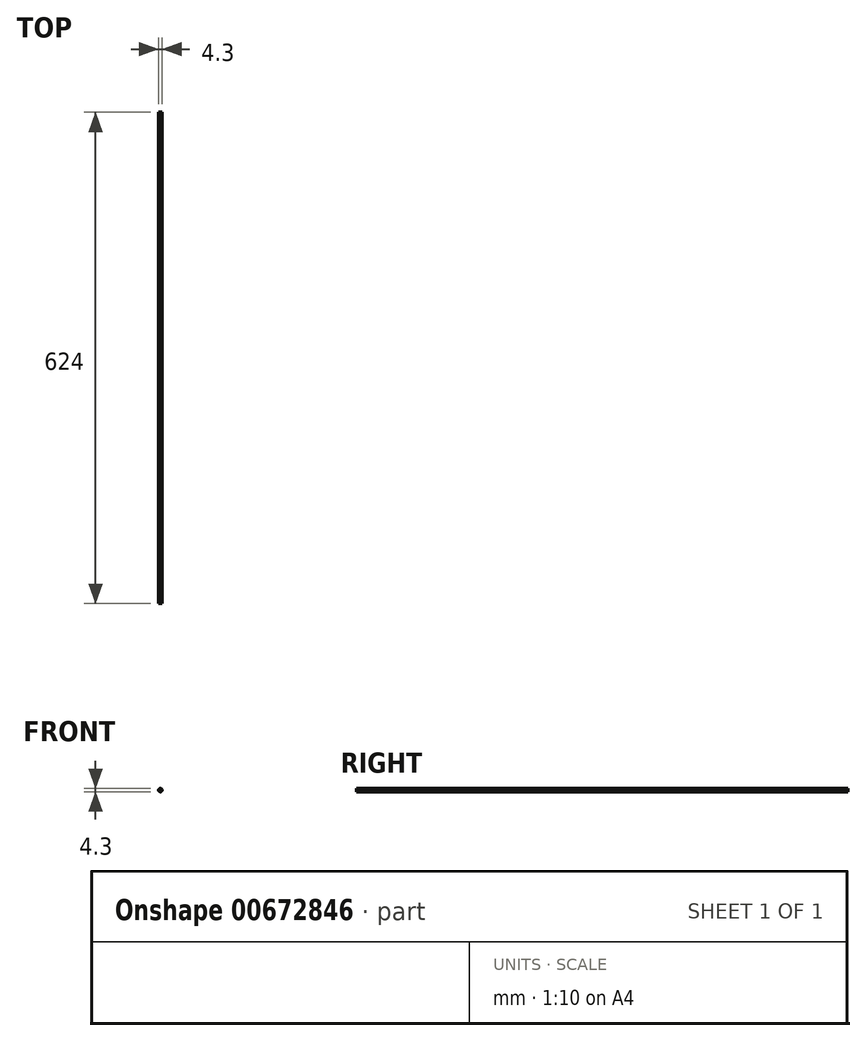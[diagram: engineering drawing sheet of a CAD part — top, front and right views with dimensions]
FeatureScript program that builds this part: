
annotation { "Feature Type Name" : "Feature", "Feature Type Description" : "" }
export const myFeature = defineFeature(function(context is Context, id is Id, definition is map)
    precondition{}
    {
        {
            var Q0;
            Q0=qCreatedBy(makeId("Front.planeOp"),FACE);
            var sketch = newSketch(context, id + "F0", { "sketchPlane" : qUnion([Q0])});
            skCircle(sketch, "E0", {"center": v(0.34, 6.3) * mm, "radius": 2.15 * mm});
            skLineSegment(sketch, "E1", {"start": v(4.5, 11.25) * mm, "end": v(4.5, 14.5) * mm});
            skArc(sketch, "E2", {"start": v(4.5, 14.5) * mm, "mid": v(4.4, 14.72) * mm, "end": v(4.2, 14.8) * mm});
            skLineSegment(sketch, "E3", {"start": v(4.2, 14.8) * mm, "end": v(3.3, 14.8) * mm});
            skArc(sketch, "E4", {"start": v(3.3, 14.8) * mm, "mid": v(3.08, 14.9) * mm, "end": v(3, 15.1) * mm});
            skLineSegment(sketch, "E5", {"start": v(3, 15.1) * mm, "end": v(3, 16) * mm});
            skArc(sketch, "E6", {"start": v(3, 16) * mm, "mid": v(3.08, 16.22) * mm, "end": v(3.3, 16.3) * mm});
            skLineSegment(sketch, "E7", {"start": v(3.3, 16.3) * mm, "end": v(10.04, 16.3) * mm});
            skArc(sketch, "E8", {"start": v(10.04, 16.3) * mm, "mid": v(10.25, 16.22) * mm, "end": v(10.34, 16) * mm});
            skLineSegment(sketch, "E9", {"start": v(10.34, 16) * mm, "end": v(10.34, 9.26) * mm});
            skArc(sketch, "E10", {"start": v(10.34, 9.26) * mm, "mid": v(10.25, 9.05) * mm, "end": v(10.04, 8.96) * mm});
            skLineSegment(sketch, "E11", {"start": v(10.04, 8.96) * mm, "end": v(9.14, 8.96) * mm});
            skArc(sketch, "E12", {"start": v(9.14, 8.96) * mm, "mid": v(8.93, 9.05) * mm, "end": v(8.84, 9.26) * mm});
            skLineSegment(sketch, "E13", {"start": v(8.84, 9.26) * mm, "end": v(8.84, 10.16) * mm});
            skArc(sketch, "E14", {"start": v(8.84, 10.16) * mm, "mid": v(8.75, 10.37) * mm, "end": v(8.54, 10.46) * mm});
            skLineSegment(sketch, "E15", {"start": v(8.54, 10.46) * mm, "end": v(5.28, 10.46) * mm});
            skArc(sketch, "E16", {"start": v(5.28, 10.46) * mm, "mid": v(5.15, 10.43) * mm, "end": v(5.05, 10.35) * mm});
            skArc(sketch, "E17", {"start": v(5.05, 10.35) * mm, "mid": v(4.06, 8.6) * mm, "end": v(3.65, 6.62) * mm});
            skLineSegment(sketch, "E18", {"start": v(3.65, 6.62) * mm, "end": v(3.34, 6.3) * mm});
            skLineSegment(sketch, "E19", {"start": v(3.34, 6.3) * mm, "end": v(3.65, 6) * mm});
            skArc(sketch, "E20", {"start": v(3.65, 6) * mm, "mid": v(4.06, 4.03) * mm, "end": v(5.05, 2.27) * mm});
            skArc(sketch, "E21", {"start": v(5.05, 2.27) * mm, "mid": v(5.15, 2.19) * mm, "end": v(5.28, 2.16) * mm});
            skLineSegment(sketch, "E22", {"start": v(5.28, 2.16) * mm, "end": v(8.54, 2.16) * mm});
            skArc(sketch, "E23", {"start": v(8.54, 2.16) * mm, "mid": v(8.75, 2.25) * mm, "end": v(8.84, 2.46) * mm});
            skLineSegment(sketch, "E24", {"start": v(8.84, 2.46) * mm, "end": v(8.84, 3.36) * mm});
            skArc(sketch, "E25", {"start": v(8.84, 3.36) * mm, "mid": v(8.93, 3.57) * mm, "end": v(9.14, 3.66) * mm});
            skLineSegment(sketch, "E26", {"start": v(9.14, 3.66) * mm, "end": v(10.04, 3.66) * mm});
            skArc(sketch, "E27", {"start": v(10.04, 3.66) * mm, "mid": v(10.25, 3.57) * mm, "end": v(10.34, 3.36) * mm});
            skLineSegment(sketch, "E28", {"start": v(10.34, 3.36) * mm, "end": v(10.34, -3.4) * mm});
            skArc(sketch, "E29", {"start": v(10.34, -3.4) * mm, "mid": v(10.25, -3.6) * mm, "end": v(10.04, -3.7) * mm});
            skLineSegment(sketch, "E30", {"start": v(10.04, -3.7) * mm, "end": v(3.3, -3.7) * mm});
            skArc(sketch, "E31", {"start": v(3.3, -3.7) * mm, "mid": v(3.08, -3.6) * mm, "end": v(3, -3.4) * mm});
            skLineSegment(sketch, "E32", {"start": v(3, -3.4) * mm, "end": v(3, -2.5) * mm});
            skArc(sketch, "E33", {"start": v(3, -2.5) * mm, "mid": v(3.08, -2.28) * mm, "end": v(3.3, -2.2) * mm});
            skLineSegment(sketch, "E34", {"start": v(3.3, -2.2) * mm, "end": v(4.2, -2.2) * mm});
            skArc(sketch, "E35", {"start": v(4.2, -2.2) * mm, "mid": v(4.4, -2.1) * mm, "end": v(4.5, -1.9) * mm});
            skLineSegment(sketch, "E36", {"start": v(4.5, -1.9) * mm, "end": v(4.5, 1.37) * mm});
            skArc(sketch, "E37", {"start": v(4.5, 1.37) * mm, "mid": v(4.46, 1.5) * mm, "end": v(4.38, 1.6) * mm});
            skArc(sketch, "E38", {"start": v(4.38, 1.6) * mm, "mid": v(2.62, 2.6) * mm, "end": v(0.65, 3) * mm});
            skLineSegment(sketch, "E39", {"start": v(0.65, 3) * mm, "end": v(0.34, 3.3) * mm});
            skLineSegment(sketch, "E40", {"start": v(0.34, 3.3) * mm, "end": v(0.03, 3) * mm});
            skArc(sketch, "E41", {"start": v(0.03, 3) * mm, "mid": v(-1.94, 2.6) * mm, "end": v(-3.7, 1.6) * mm});
            skArc(sketch, "E42", {"start": v(-3.7, 1.6) * mm, "mid": v(-3.78, 1.5) * mm, "end": v(-3.8, 1.37) * mm});
            skLineSegment(sketch, "E43", {"start": v(-3.8, 1.37) * mm, "end": v(-3.8, -1.9) * mm});
            skArc(sketch, "E44", {"start": v(-3.8, -1.9) * mm, "mid": v(-3.72, -2.1) * mm, "end": v(-3.5, -2.2) * mm});
            skLineSegment(sketch, "E45", {"start": v(-3.5, -2.2) * mm, "end": v(-2.6, -2.2) * mm});
            skArc(sketch, "E46", {"start": v(-2.6, -2.2) * mm, "mid": v(-2.4, -2.28) * mm, "end": v(-2.3, -2.5) * mm});
            skLineSegment(sketch, "E47", {"start": v(-2.3, -2.5) * mm, "end": v(-2.3, -3.4) * mm});
            skArc(sketch, "E48", {"start": v(-2.3, -3.4) * mm, "mid": v(-2.4, -3.6) * mm, "end": v(-2.6, -3.7) * mm});
            skLineSegment(sketch, "E49", {"start": v(-2.6, -3.7) * mm, "end": v(-9.36, -3.7) * mm});
            skArc(sketch, "E50", {"start": v(-9.36, -3.7) * mm, "mid": v(-9.57, -3.6) * mm, "end": v(-9.66, -3.4) * mm});
            skLineSegment(sketch, "E51", {"start": v(-9.66, -3.4) * mm, "end": v(-9.66, 3.36) * mm});
            skArc(sketch, "E52", {"start": v(-9.66, 3.36) * mm, "mid": v(-9.57, 3.57) * mm, "end": v(-9.36, 3.66) * mm});
            skLineSegment(sketch, "E53", {"start": v(-9.36, 3.66) * mm, "end": v(-8.46, 3.66) * mm});
            skArc(sketch, "E54", {"start": v(-8.46, 3.66) * mm, "mid": v(-8.25, 3.57) * mm, "end": v(-8.16, 3.36) * mm});
            skLineSegment(sketch, "E55", {"start": v(-8.16, 3.36) * mm, "end": v(-8.16, 2.46) * mm});
            skArc(sketch, "E56", {"start": v(-8.16, 2.46) * mm, "mid": v(-8.07, 2.25) * mm, "end": v(-7.86, 2.16) * mm});
            skLineSegment(sketch, "E57", {"start": v(-7.86, 2.16) * mm, "end": v(-4.6, 2.16) * mm});
            skArc(sketch, "E58", {"start": v(-4.6, 2.16) * mm, "mid": v(-4.47, 2.19) * mm, "end": v(-4.37, 2.27) * mm});
            skArc(sketch, "E59", {"start": v(-4.37, 2.27) * mm, "mid": v(-3.37, 4.03) * mm, "end": v(-2.97, 6) * mm});
            skLineSegment(sketch, "E60", {"start": v(-2.97, 6) * mm, "end": v(-2.66, 6.3) * mm});
            skLineSegment(sketch, "E61", {"start": v(-2.66, 6.3) * mm, "end": v(-2.97, 6.62) * mm});
            skArc(sketch, "E62", {"start": v(-2.97, 6.62) * mm, "mid": v(-3.37, 8.6) * mm, "end": v(-4.37, 10.35) * mm});
            skArc(sketch, "E63", {"start": v(-4.37, 10.35) * mm, "mid": v(-4.47, 10.43) * mm, "end": v(-4.6, 10.46) * mm});
            skLineSegment(sketch, "E64", {"start": v(-4.6, 10.46) * mm, "end": v(-7.86, 10.46) * mm});
            skArc(sketch, "E65", {"start": v(-7.86, 10.46) * mm, "mid": v(-8.07, 10.37) * mm, "end": v(-8.16, 10.16) * mm});
            skLineSegment(sketch, "E66", {"start": v(-8.16, 10.16) * mm, "end": v(-8.16, 9.26) * mm});
            skArc(sketch, "E67", {"start": v(-8.16, 9.26) * mm, "mid": v(-8.25, 9.05) * mm, "end": v(-8.46, 8.96) * mm});
            skLineSegment(sketch, "E68", {"start": v(-8.46, 8.96) * mm, "end": v(-9.36, 8.96) * mm});
            skArc(sketch, "E69", {"start": v(-9.36, 8.96) * mm, "mid": v(-9.57, 9.05) * mm, "end": v(-9.66, 9.26) * mm});
            skLineSegment(sketch, "E70", {"start": v(-9.66, 9.26) * mm, "end": v(-9.66, 16) * mm});
            skArc(sketch, "E71", {"start": v(-9.66, 16) * mm, "mid": v(-9.57, 16.22) * mm, "end": v(-9.36, 16.3) * mm});
            skLineSegment(sketch, "E72", {"start": v(-9.36, 16.3) * mm, "end": v(-2.6, 16.3) * mm});
            skArc(sketch, "E73", {"start": v(-2.6, 16.3) * mm, "mid": v(-2.4, 16.22) * mm, "end": v(-2.3, 16) * mm});
            skLineSegment(sketch, "E74", {"start": v(-2.3, 16) * mm, "end": v(-2.3, 15.1) * mm});
            skArc(sketch, "E75", {"start": v(-2.3, 15.1) * mm, "mid": v(-2.4, 14.9) * mm, "end": v(-2.6, 14.8) * mm});
            skLineSegment(sketch, "E76", {"start": v(-2.6, 14.8) * mm, "end": v(-3.5, 14.8) * mm});
            skArc(sketch, "E77", {"start": v(-3.5, 14.8) * mm, "mid": v(-3.72, 14.72) * mm, "end": v(-3.8, 14.5) * mm});
            skLineSegment(sketch, "E78", {"start": v(-3.8, 14.5) * mm, "end": v(-3.8, 11.25) * mm});
            skArc(sketch, "E79", {"start": v(-3.8, 11.25) * mm, "mid": v(-3.78, 11.12) * mm, "end": v(-3.7, 11.02) * mm});
            skArc(sketch, "E80", {"start": v(-3.7, 11.02) * mm, "mid": v(-1.94, 10.02) * mm, "end": v(0.03, 9.62) * mm});
            skLineSegment(sketch, "E81", {"start": v(0.03, 9.62) * mm, "end": v(0.34, 9.3) * mm});
            skLineSegment(sketch, "E82", {"start": v(0.34, 9.3) * mm, "end": v(0.65, 9.62) * mm});
            skArc(sketch, "E83", {"start": v(0.65, 9.62) * mm, "mid": v(2.62, 10.02) * mm, "end": v(4.38, 11.02) * mm});
            skArc(sketch, "E84", {"start": v(4.38, 11.02) * mm, "mid": v(4.46, 11.12) * mm, "end": v(4.5, 11.25) * mm});
            skCircle(sketch, "E85", {"center": v(-6.66, 13.3) * mm, "radius": 2 * mm});
            skCircle(sketch, "E86", {"center": v(-6.66, -0.7) * mm, "radius": 2 * mm});
            skCircle(sketch, "E87", {"center": v(7.34, 13.3) * mm, "radius": 2 * mm});
            skCircle(sketch, "E88", {"center": v(7.34, -0.7) * mm, "radius": 2 * mm});
            skSolve(sketch);
        }
        {
            var Q0;
            Q0=makeQuery(id+"F0.imprint","IMPRINT",FACE,{"disambiguationData":[TD([[makeQuery(id+"F0.imprint","IMPRINT",EDGE,{"derivedFrom":sQuery(id+"F0.wireOp",EDGE,"E0")}),1.0]])]});
            extrude(context, id + "F1", {"entities" : qUnion([Q0]), "endBound" : BoundingType.SYMMETRIC, "depth" : 624 * mm, "offsetDistance" : 25 * mm});
        }
    });
